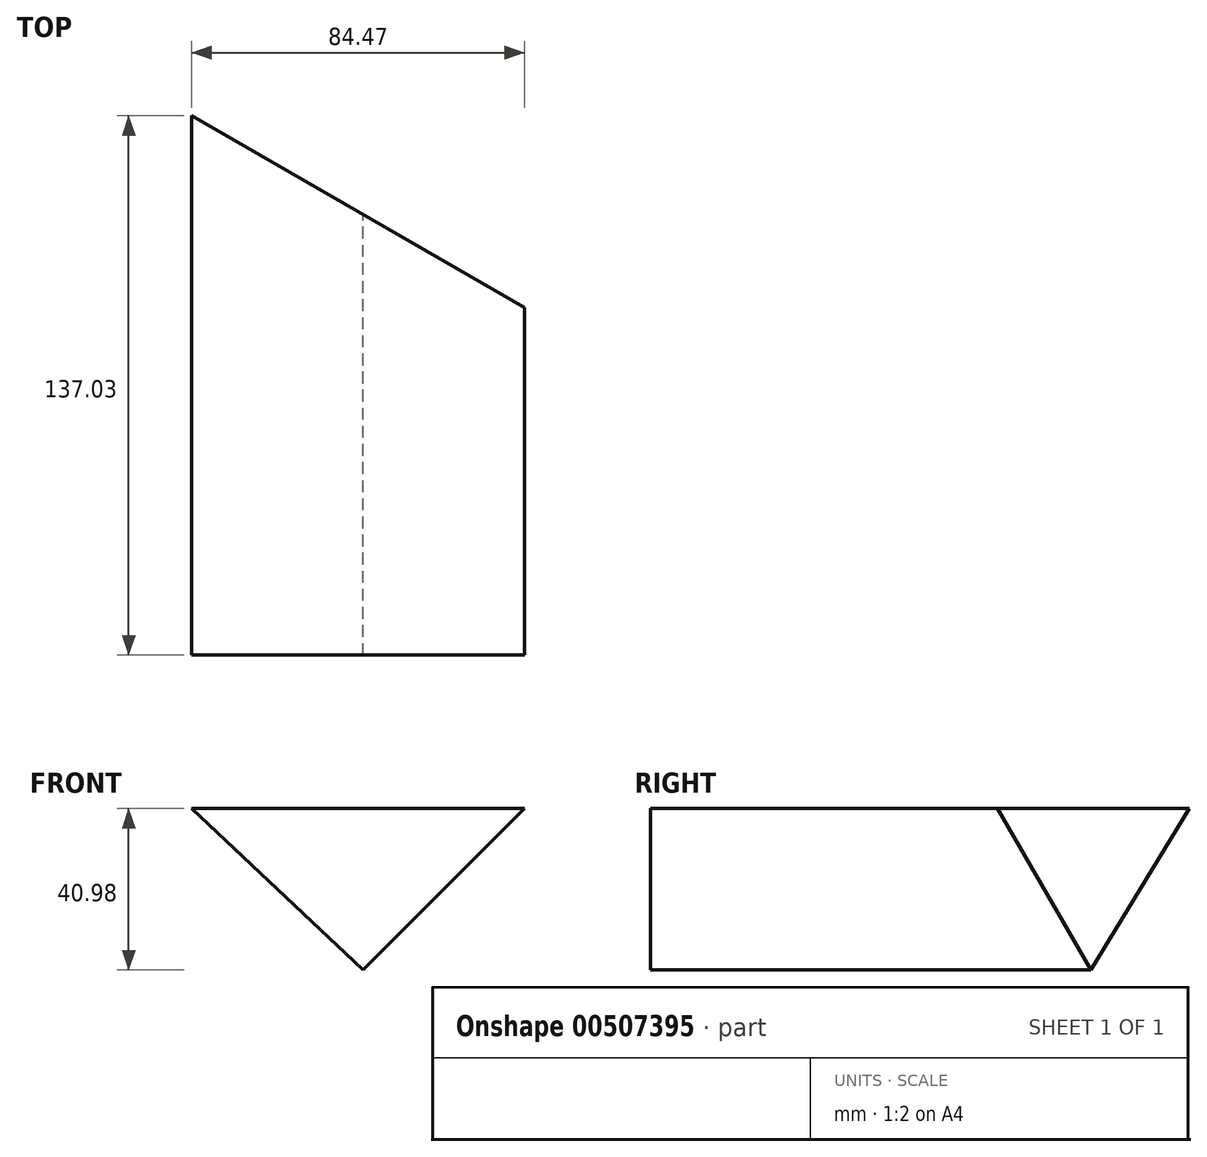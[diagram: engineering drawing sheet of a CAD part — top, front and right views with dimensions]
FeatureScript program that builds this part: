
annotation { "Feature Type Name" : "Feature", "Feature Type Description" : "" }
export const myFeature = defineFeature(function(context is Context, id is Id, definition is map)
    precondition{}
    {
        {
            var Q0;
            Q0=qCreatedBy(makeId("Front.planeOp"),FACE);
            var sketch = newSketch(context, id + "F0", { "sketchPlane" : qUnion([Q0])});
            skLineSegment(sketch, "E0", {"start": v(0, 0) * mm, "end": v(40.98, 40.98) * mm});
            skLineSegment(sketch, "E1", {"start": v(40.98, 40.98) * mm, "end": v(-43.49, 40.98) * mm});
            skLineSegment(sketch, "E2", {"start": v(-43.49, 40.98) * mm, "end": v(0, 0) * mm});
            skSolve(sketch);
        }
        {
            var Q0;
            Q0 = qSketchRegion(id + "F0", true);
            extrude(context, id + "F1", {"entities" : qUnion([Q0]), "depth" : 254 * mm});
        }
        {
            var Q0;
            Q0=makeQuery(id+"F1.opExtrude","SWEPT_FACE",FACE,{"disambiguationData":[OSD([sQuery(id+"F0.wireOp",EDGE,"E1")])]});
            var sketch = newSketch(context, id + "F2", { "sketchPlane" : qUnion([Q0])});
            skLineSegment(sketch, "E3", {"start": v(-43.49, -116.97) * mm, "end": v(40.98, -165.74) * mm});
            skLineSegment(sketch, "E4", {"start": v(40.98, -165.74) * mm, "end": v(40.98, 0) * mm});
            skLineSegment(sketch, "E5", {"start": v(40.98, 0) * mm, "end": v(-43.49, 0) * mm});
            skLineSegment(sketch, "E6", {"start": v(-43.49, 0) * mm, "end": v(-43.49, -116.97) * mm});
            skSolve(sketch);
        }
        {
            var Q0;
            Q0 = qSketchRegion(id + "F2", true);
            extrude(context, id + "F3", {"entities" : qUnion([Q0]), "operationType" : NewBodyOperationType.REMOVE, "endBound" : BoundingType.THROUGH_ALL, "oppositeDirection" : true, "depth" : 25.4 * mm});
        }
    });
